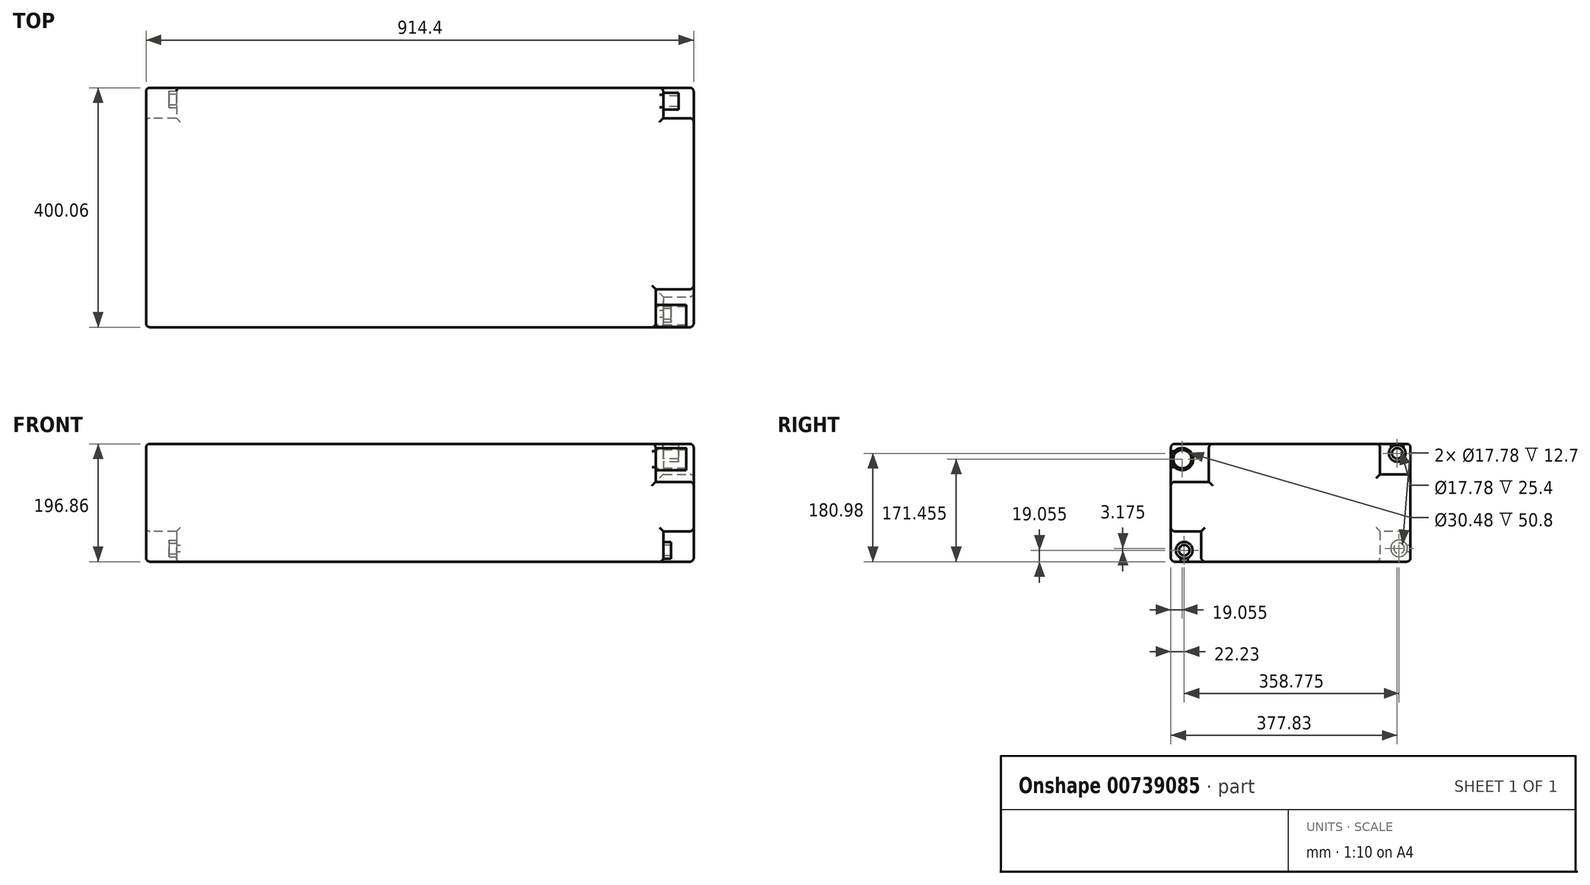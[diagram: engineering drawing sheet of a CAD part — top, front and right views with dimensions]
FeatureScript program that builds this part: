
annotation { "Feature Type Name" : "Feature", "Feature Type Description" : "" }
export const myFeature = defineFeature(function(context is Context, id is Id, definition is map)
    precondition{}
    {
        {
            var Q0;
            Q0=qCreatedBy(makeId("Top.planeOp"),FACE);
            var sketch = newSketch(context, id + "F0", { "sketchPlane" : qUnion([Q0])});
            skLineSegment(sketch, "E0.bottom", {"start": v(-457.2, 200.03) * mm, "end": v(457.2, 200.03) * mm});
            skLineSegment(sketch, "E0.top", {"start": v(-457.2, -200.02) * mm, "end": v(457.2, -200.02) * mm});
            skLineSegment(sketch, "E0.left", {"start": v(-457.2, 200.03) * mm, "end": v(-457.2, -200.02) * mm});
            skLineSegment(sketch, "E0.right", {"start": v(457.2, 200.03) * mm, "end": v(457.2, -200.02) * mm});
            skPoint(sketch, "E0.middle", {"position": v(0, 0) * mm});
            skSolve(sketch);
        }
        {
            var Q0;
            Q0=qSketchRegion(id+"F0",true);
            extrude(context, id + "F1", {"entities" : qUnion([Q0]), "endBound" : BoundingType.SYMMETRIC, "depth" : 196.85 * mm, "offsetDistance" : 25.4 * mm});
        }
        {
            var Q0;
            Q0=makeQuery(id+"F1.opExtrude","SWEPT_FACE",FACE,{"disambiguationData":[OSD([sQuery(id+"F0.wireOp",EDGE,"E0.right")])]});
            var sketch = newSketch(context, id + "F2", { "sketchPlane" : qUnion([Q0])});
            skLineSegment(sketch, "E1", {"start": v(-200.02, -47.63) * mm, "end": v(-149.22, -47.63) * mm});
            skLineSegment(sketch, "E2", {"start": v(-149.22, -47.63) * mm, "end": v(-149.22, -98.43) * mm});
            skLineSegment(sketch, "E3", {"start": v(-200.02, 34.93) * mm, "end": v(-136.52, 34.93) * mm});
            skLineSegment(sketch, "E4", {"start": v(-136.52, 34.93) * mm, "end": v(-136.52, 98.43) * mm});
            skLineSegment(sketch, "E5", {"start": v(149.23, 98.43) * mm, "end": v(149.23, 47.63) * mm});
            skLineSegment(sketch, "E6", {"start": v(149.23, 47.63) * mm, "end": v(200.03, 47.63) * mm});
            skSolve(sketch);
        }
        {
            var Q0;
            {var subQ0=sQuery(id+"F2.wireOp",EDGE,"E1");Q0=makeQuery(id+"F2.imprint","IMPRINT",FACE,{"disambiguationData":[TD([[makeQuery(id+"F2.imprint","IMPRINT",EDGE,{"derivedFrom":subQ0}),-1.0]])]});}
            var Q1;
            {var subQ0=sQuery(id+"F2.wireOp",EDGE,"E5");Q1=makeQuery(id+"F2.imprint","IMPRINT",FACE,{"disambiguationData":[TD([[makeQuery(id+"F2.imprint","IMPRINT",EDGE,{"derivedFrom":subQ0}),1.0]])]});}
            extrude(context, id + "F3", {"entities" : qUnion([Q0, Q1]), "operationType" : NewBodyOperationType.REMOVE, "oppositeDirection" : true, "depth" : 50.8 * mm, "offsetDistance" : 25.4 * mm});
        }
        {
            var Q0;
            {var subQ0=sQuery(id+"F2.wireOp",EDGE,"E3");Q0=makeQuery(id+"F2.imprint","IMPRINT",FACE,{"disambiguationData":[TD([[makeQuery(id+"F2.imprint","IMPRINT",EDGE,{"derivedFrom":subQ0}),1.0]])]});}
            extrude(context, id + "F4", {"entities" : qUnion([Q0]), "operationType" : NewBodyOperationType.REMOVE, "oppositeDirection" : true, "depth" : 63.5 * mm, "offsetDistance" : 25.4 * mm});
        }
        {
            var Q0;
            Q0=makeQuery(id+"F1.opExtrude","SWEPT_FACE",FACE,{"disambiguationData":[OSD([sQuery(id+"F0.wireOp",EDGE,"E0.left")])]});
            var sketch = newSketch(context, id + "F5", { "sketchPlane" : qUnion([Q0])});
            skLineSegment(sketch, "E7", {"start": v(-200.03, -47.63) * mm, "end": v(-149.22, -47.63) * mm});
            skLineSegment(sketch, "E8", {"start": v(-149.22, -47.63) * mm, "end": v(-149.22, -98.43) * mm});
            skSolve(sketch);
        }
        {
            var Q0;
            {var subQ0=sQuery(id+"F5.wireOp",EDGE,"E7");Q0=makeQuery(id+"F5.imprint","IMPRINT",FACE,{"disambiguationData":[TD([[makeQuery(id+"F5.imprint","IMPRINT",EDGE,{"derivedFrom":subQ0}),-1.0]])]});}
            extrude(context, id + "F6", {"entities" : qUnion([Q0]), "operationType" : NewBodyOperationType.REMOVE, "oppositeDirection" : true, "depth" : 50.8 * mm, "offsetDistance" : 25.4 * mm});
        }
        {
            var Q0;
            Q0=makeQuery(id+"F3.boolean.opBoolean","COPY",FACE,{"derivedFrom":makeQuery(id+"F3.opExtrude","CAP_FACE",FACE,{"disambiguationData":[OSD([sQuery(id+"F0.wireOp",EDGE,"E0.bottom"),sQuery(id+"F0.wireOp",EDGE,"E0.right"),sQuery(id+"F2.wireOp",EDGE,"E5"),sQuery(id+"F2.wireOp",EDGE,"E6")])],"isStart":false})});
            var sketch = newSketch(context, id + "F7", { "sketchPlane" : qUnion([Q0])});
            skCircle(sketch, "E9", {"center": v(177.8, 82.55) * mm, "radius": 13.97 * mm});
            skCircle(sketch, "E10", {"center": v(177.8, 82.55) * mm, "radius": 8.9 * mm});
            skCircle(sketch, "E11", {"center": v(-177.8, -79.38) * mm, "radius": 8.9 * mm});
            skCircle(sketch, "E12", {"center": v(-177.8, -79.38) * mm, "radius": 13.97 * mm});
            skSolve(sketch);
        }
        {
            var Q0;
            Q0=makeQuery(id+"F7.imprint","IMPRINT",FACE,{"disambiguationData":[TD([[makeQuery(id+"F7.imprint","IMPRINT",EDGE,{"derivedFrom":sQuery(id+"F7.wireOp",EDGE,"E9")}),1.0]])]});
            extrude(context, id + "F8", {"entities" : qUnion([Q0]), "operationType" : NewBodyOperationType.ADD, "depth" : 25.4 * mm, "offsetDistance" : 25.4 * mm});
        }
        {
            var Q0;
            Q0=makeQuery(id+"F6.boolean.opBoolean","COPY",FACE,{"derivedFrom":makeQuery(id+"F6.opExtrude","CAP_FACE",FACE,{"disambiguationData":[OSD([sQuery(id+"F0.wireOp",EDGE,"E0.bottom"),sQuery(id+"F0.wireOp",EDGE,"E0.left"),sQuery(id+"F5.wireOp",EDGE,"E7"),sQuery(id+"F5.wireOp",EDGE,"E8")])],"isStart":false})});
            var sketch = newSketch(context, id + "F9", { "sketchPlane" : qUnion([Q0])});
            skCircle(sketch, "E13", {"center": v(-180.98, -76.2) * mm, "radius": 13.97 * mm});
            skCircle(sketch, "E14", {"center": v(-180.98, -76.2) * mm, "radius": 8.9 * mm});
            skSolve(sketch);
        }
        {
            var Q0;
            Q0=qSketchRegion(id+"F9",true);
            extrude(context, id + "F10", {"entities" : qUnion([Q0]), "operationType" : NewBodyOperationType.ADD, "depth" : 12.7 * mm, "offsetDistance" : 25.4 * mm});
        }
        {
            var Q0;
            Q0=qSketchRegion(id+"F7",true);
            extrude(context, id + "F11", {"entities" : qUnion([Q0]), "operationType" : NewBodyOperationType.ADD, "depth" : 12.7 * mm, "offsetDistance" : 25.4 * mm});
        }
        {
            var Q0;
            Q0=makeQuery(id+"F4.boolean.opBoolean","COPY",FACE,{"derivedFrom":makeQuery(id+"F4.opExtrude","CAP_FACE",FACE,{"disambiguationData":[OSD([sQuery(id+"F0.wireOp",EDGE,"E0.top"),sQuery(id+"F0.wireOp",EDGE,"E0.right"),sQuery(id+"F2.wireOp",EDGE,"E3"),sQuery(id+"F2.wireOp",EDGE,"E4")])],"isStart":false})});
            var sketch = newSketch(context, id + "F12", { "sketchPlane" : qUnion([Q0])});
            skCircle(sketch, "E15", {"center": v(-180.97, 73.03) * mm, "radius": 18.41 * mm});
            skCircle(sketch, "E16", {"center": v(-180.97, 73.03) * mm, "radius": 15.24 * mm});
            skSolve(sketch);
        }
        {
            var Q0;
            Q0=qSketchRegion(id+"F12",true);
            extrude(context, id + "F13", {"entities" : qUnion([Q0]), "operationType" : NewBodyOperationType.ADD, "depth" : 50.8 * mm, "offsetDistance" : 25.4 * mm});
        }
        {
            var Q0;
            Q0=makeQuery(id+"F1.opExtrude","SWEPT_FACE",FACE,{"disambiguationData":[OSD([sQuery(id+"F0.wireOp",EDGE,"E0.right")])]});
            var Q1;
            Q1=makeQuery(id+"F1.opExtrude","SWEPT_FACE",FACE,{"disambiguationData":[OSD([sQuery(id+"F0.wireOp",EDGE,"E0.bottom")])]});
            var Q2;
            Q2=makeQuery(id+"F1.opExtrude","CAP_FACE",FACE,{"disambiguationData":[OSD([sQuery(id+"F0.wireOp",EDGE,"E0.bottom"),sQuery(id+"F0.wireOp",EDGE,"E0.top"),sQuery(id+"F0.wireOp",EDGE,"E0.left"),sQuery(id+"F0.wireOp",EDGE,"E0.right")])],"isStart":true});
            var Q3;
            Q3=makeQuery(id+"F1.opExtrude","CAP_FACE",FACE,{"disambiguationData":[OSD([sQuery(id+"F0.wireOp",EDGE,"E0.bottom"),sQuery(id+"F0.wireOp",EDGE,"E0.top"),sQuery(id+"F0.wireOp",EDGE,"E0.left"),sQuery(id+"F0.wireOp",EDGE,"E0.right")])],"isStart":false});
            var Q4;
            Q4=makeQuery(id+"F1.opExtrude","SWEPT_FACE",FACE,{"disambiguationData":[OSD([sQuery(id+"F0.wireOp",EDGE,"E0.left")])]});
            var Q5;
            Q5=makeQuery(id+"F1.opExtrude","SWEPT_FACE",FACE,{"disambiguationData":[OSD([sQuery(id+"F0.wireOp",EDGE,"E0.top")])]});
            fillet(context, id + "F14", {"entities" : qUnion([Q0, Q1, Q2, Q3, Q4, Q5]), "radius" : 6.35 * mm, "tangentPropagation" : true, "allowEdgeOverflow" : false});
        }
    });
